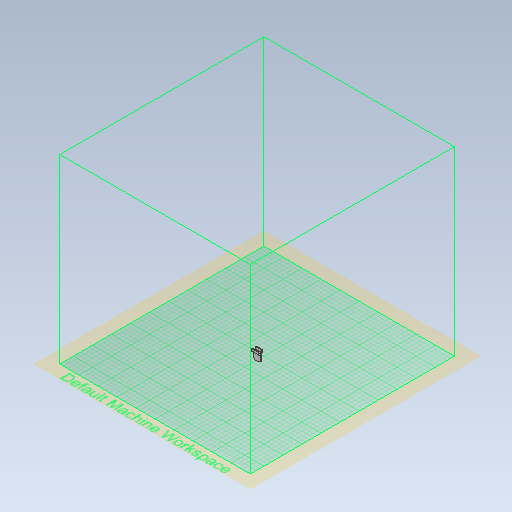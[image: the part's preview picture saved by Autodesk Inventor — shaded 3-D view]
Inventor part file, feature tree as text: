
AUTODESK INVENTOR PART (.ipt)
format: ipt  version: 2020 (Build 240168000, 168)  size: 411,648 bytes
history: native  units: mm
features: extrude x6, sketch x6, fillet x4, plane x1
ambient origin geometry x8: Origin, YZ Plane, XZ Plane, XY Plane, X Axis, Y Axis, Z Axis, Center Point
bodies: Solid1 (feature_tree)
feature tree (17):
  extrude  "Extrusion1"  Depth=14.0mm
  extrude  "Extrusion2"  Depth=10.0mm
  fillet  "Fillet8"  Radius=2.0mm
  extrude  "Extrusion3"  Depth=0.5mm TaperAngle=0.0deg
  fillet  "Fillet9"  Radius=0.5mm
  plane  "Work Plane1"
  sketch  "Sketch6"  dims[d19=2.5mm d20=2.5mm]
  extrude  "Extrusion4"  Depth=2.5mm
  sketch  "Sketch7"  dims[d24=1.899691mm d25=14.0mm d26=0.0mm d27=2.5mm d28=0.5mm]
  extrude  "Extrusion5"  Depth=14.0mm TaperAngle=0.0deg
  fillet  "Fillet11"  Radius=2.5mm
  fillet  "Fillet12"  Radius=0.5mm
  extrude  "Extrusion6"  Depth=1.0mm TaperAngle=0.0deg
  sketch  "Sketch1"  dims[d0=14.0mm d1=7.5mm]
  sketch  "Sketch2"  dims[d2=10.0mm d3=0.0mm d4=6.0mm d5=2.0mm]
  sketch  "Sketch3"  dims[d6=2.0mm d7=5.5mm d8=0.0mm d16=0.5mm]
  sketch  "Sketch8"  dims[d29=2.8mm d30=0.0mm d31=1.0mm d32=0.0mm d34=1.0mm d35=1.0mm d36=2.8mm d37=0.0mm d40=1.0mm d41=1.0mm]
